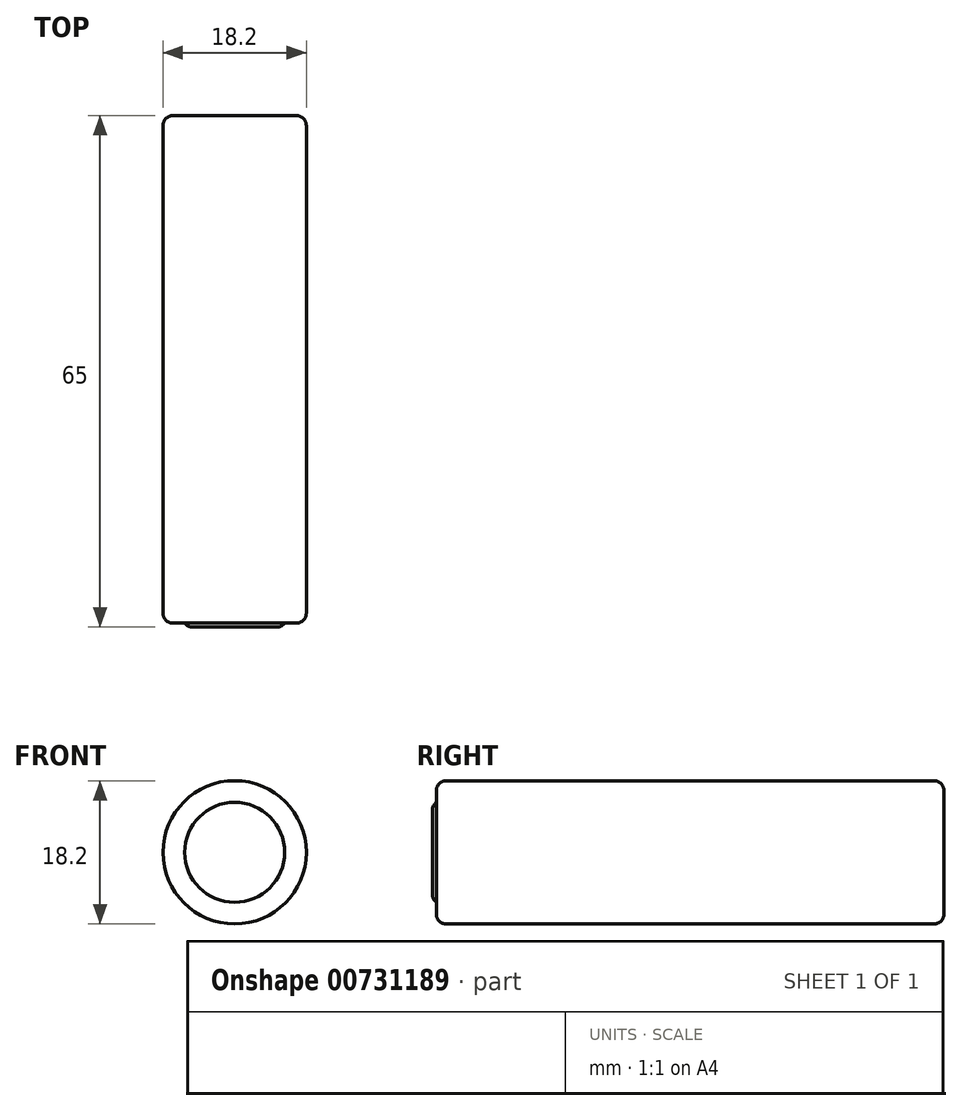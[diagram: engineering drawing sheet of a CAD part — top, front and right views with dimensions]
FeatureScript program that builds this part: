
annotation { "Feature Type Name" : "Feature", "Feature Type Description" : "" }
export const myFeature = defineFeature(function(context is Context, id is Id, definition is map)
    precondition{}
    {
        {
            var Q0;
            Q0=qCreatedBy(makeId("Front.planeOp"),FACE);
            var sketch = newSketch(context, id + "F0", { "sketchPlane" : qUnion([Q0])});
            skCircle(sketch, "E0", {"center": v(0, 0) * mm, "radius": 9.1 * mm});
            skSolve(sketch);
        }
        {
            var Q0;
            Q0 = qSketchRegion(id + "F0", true);
            extrude(context, id + "F1", {"entities" : qUnion([Q0]), "oppositeDirection" : true, "depth" : 64.5 * mm, "offsetDistance" : 25.4 * mm});
        }
        {
            var Q0;
            Q0=makeQuery(id+"F1.opExtrude","CAP_FACE",FACE,{"disambiguationData":[OSD([sQuery(id+"F0.wireOp",EDGE,"E0")])],"isStart":true});
            var sketch = newSketch(context, id + "F2", { "sketchPlane" : qUnion([Q0])});
            skCircle(sketch, "E1", {"center": v(0, 0) * mm, "radius": 6.35 * mm});
            skSolve(sketch);
        }
        {
            var Q0;
            Q0 = qSketchRegion(id + "F2", true);
            extrude(context, id + "F3", {"entities" : qUnion([Q0]), "operationType" : NewBodyOperationType.ADD, "depth" : 0.5 * mm, "offsetDistance" : 25.4 * mm});
        }
        {
            var Q0;
            Q0=makeQuery(id+"F1.opExtrude","CAP_EDGE",EDGE,{"disambiguationData":[OSD([sQuery(id+"F0.wireOp",EDGE,"E0")])],"isStart":false});
            var Q1;
            Q1=makeQuery(id+"F1.opExtrude","CAP_EDGE",EDGE,{"disambiguationData":[OSD([sQuery(id+"F0.wireOp",EDGE,"E0")])],"isStart":true});
            var Q2;
            Q2=makeQuery(id+"F3.opExtrude","CAP_EDGE",EDGE,{"disambiguationData":[OSD([sQuery(id+"F2.wireOp",EDGE,"E1")])],"isStart":false});
            fillet(context, id + "F4", {"entities" : qUnion([Q0, Q1, Q2]), "radius" : 1.27 * mm, "tangentPropagation" : true, "allowEdgeOverflow" : false});
        }
    });
